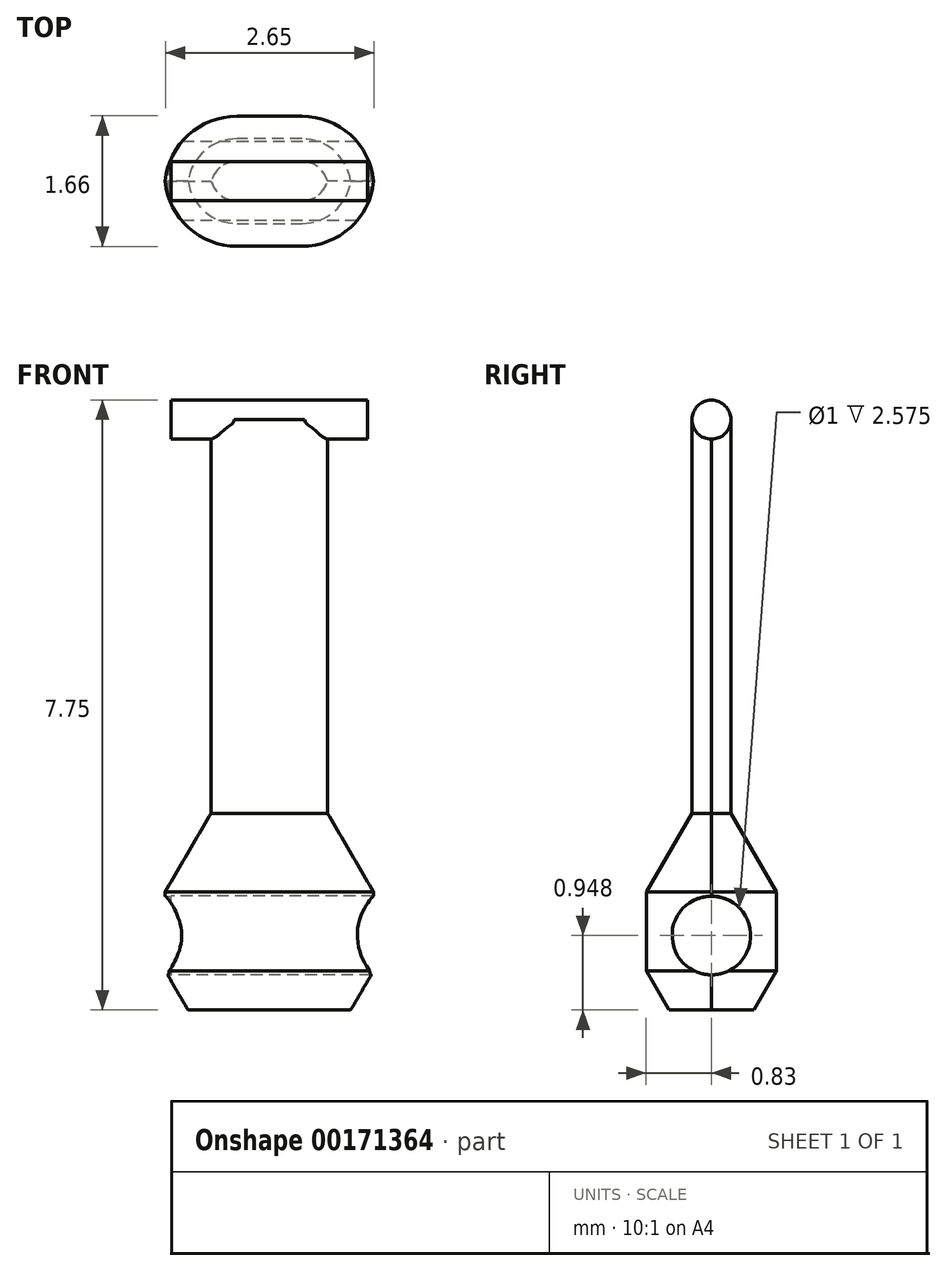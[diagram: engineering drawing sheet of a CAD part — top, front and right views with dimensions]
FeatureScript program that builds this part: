
annotation { "Feature Type Name" : "Feature", "Feature Type Description" : "" }
export const myFeature = defineFeature(function(context is Context, id is Id, definition is map)
    precondition{}
    {
        {
            var Q0;
            Q0=qCreatedBy(makeId("Right.planeOp"),FACE);
            var sketch = newSketch(context, id + "F0", { "sketchPlane" : qUnion([Q0])});
            skCircle(sketch, "E0", {"center": v(0, 0) * mm, "radius": 0.25 * mm});
            skSolve(sketch);
        }
        {
            var Q0;
            Q0=makeQuery(id+"F0.imprint","IMPRINT",FACE,{"disambiguationData":[TD([[makeQuery(id+"F0.imprint","IMPRINT",EDGE,{"derivedFrom":sQuery(id+"F0.wireOp",EDGE,"E0")}),1.0]])]});
            extrude(context, id + "F1", {"entities" : qUnion([Q0]), "depth" : 2.5 * mm});
        }
        {
            var Q0;
            Q0=qCreatedBy(makeId("Top.planeOp"),FACE);
            var sketch = newSketch(context, id + "F2", { "sketchPlane" : qUnion([Q0])});
            skPoint(sketch, "E1", {"position": v(1.25, 0) * mm});
            skPoint(sketch, "E2.start.orphan", {"position": v(0, -0.24) * mm});
            skPoint(sketch, "E3.bottom.end.orphan", {"position": v(1, 0.25) * mm});
            skPoint(sketch, "E3.left.start.orphan", {"position": v(1.5, 0.25) * mm});
            skPoint(sketch, "E3.top.end.orphan", {"position": v(1, -0.25) * mm});
            skPoint(sketch, "E3.top.start.orphan", {"position": v(1.5, -0.25) * mm});
            skLineSegment(sketch, "E4.bottom", {"start": v(2, 0.25) * mm, "end": v(0.5, 0.25) * mm});
            skLineSegment(sketch, "E4.top", {"start": v(2, -0.25) * mm, "end": v(0.5, -0.25) * mm});
            skLineSegment(sketch, "E4.left", {"start": v(2, 0.25) * mm, "end": v(2, -0.25) * mm});
            skLineSegment(sketch, "E4.right", {"start": v(0.5, 0.25) * mm, "end": v(0.5, -0.25) * mm});
            skSolve(sketch);
        }
        {
            var Q0;
            Q0 = qSketchRegion(id + "F2", true);
            extrude(context, id + "F3", {"entities" : qUnion([Q0]), "operationType" : NewBodyOperationType.ADD, "oppositeDirection" : true, "depth" : 5 * mm});
        }
        {
            var Q0;
            Q0=makeQuery(id+"F3.opExtrude","SWEPT_EDGE",EDGE,{"disambiguationData":[OSD([sQuery(id+"F2.wireOp",EDGE,"E4.top"),sQuery(id+"F2.wireOp",EDGE,"E4.right")])]});
            var Q1;
            Q1=makeQuery(id+"F3.opExtrude","SWEPT_EDGE",EDGE,{"disambiguationData":[OSD([sQuery(id+"F2.wireOp",EDGE,"E4.bottom"),sQuery(id+"F2.wireOp",EDGE,"E4.right")])]});
            var Q2;
            Q2=makeQuery(id+"F3.opExtrude","SWEPT_EDGE",EDGE,{"disambiguationData":[OSD([sQuery(id+"F2.wireOp",EDGE,"E4.bottom"),sQuery(id+"F2.wireOp",EDGE,"E4.left")])]});
            var Q3;
            Q3=makeQuery(id+"F3.opExtrude","SWEPT_EDGE",EDGE,{"disambiguationData":[OSD([sQuery(id+"F2.wireOp",EDGE,"E4.top"),sQuery(id+"F2.wireOp",EDGE,"E4.left")])]});
            fillet(context, id + "F4", {"entities" : qUnion([Q0, Q1, Q2, Q3]), "radius" : 0.34 * mm, "tangentPropagation" : true, "allowEdgeOverflow" : false});
        }
        {
            var Q0;
            Q0=makeQuery(id+"F3.opExtrude","CAP_FACE",FACE,{"disambiguationData":[OSD([sQuery(id+"F2.wireOp",EDGE,"E4.bottom"),sQuery(id+"F2.wireOp",EDGE,"E4.top"),sQuery(id+"F2.wireOp",EDGE,"E4.left"),sQuery(id+"F2.wireOp",EDGE,"E4.right")])],"isStart":false});
            extrude(context, id + "F5", {"entities" : qUnion([Q0]), "operationType" : NewBodyOperationType.ADD, "depth" : 1 * mm, "hasDraft" : true, "draftAngle" : 30 * degree});
        }
        {
            var Q0;
            Q0=makeQuery(id+"F5.opExtrude","CAP_FACE",FACE,{"disambiguationData":[OSD([sQuery(id+"F2.wireOp",EDGE,"E4.bottom"),sQuery(id+"F2.wireOp",EDGE,"E4.top"),sQuery(id+"F2.wireOp",EDGE,"E4.left"),sQuery(id+"F2.wireOp",EDGE,"E4.right")])],"isStart":false});
            extrude(context, id + "F6", {"entities" : qUnion([Q0]), "operationType" : NewBodyOperationType.ADD, "depth" : 1 * mm});
        }
        {
            var Q0;
            Q0=makeQuery(id+"F6.opExtrude","CAP_FACE",FACE,{"disambiguationData":[OSD([sQuery(id+"F2.wireOp",EDGE,"E4.bottom"),sQuery(id+"F2.wireOp",EDGE,"E4.top"),sQuery(id+"F2.wireOp",EDGE,"E4.left"),sQuery(id+"F2.wireOp",EDGE,"E4.right")])],"isStart":false});
            extrude(context, id + "F7", {"entities" : qUnion([Q0]), "operationType" : NewBodyOperationType.ADD, "depth" : 0.5 * mm, "hasDraft" : true, "draftAngle" : 30 * degree, "draftPullDirection" : true});
        }
        {
            var Q0;
            Q0=qCreatedBy(makeId("Right.planeOp"),FACE);
            var sketch = newSketch(context, id + "F8", { "sketchPlane" : qUnion([Q0])});
            skPoint(sketch, "E5", {"position": v(0, -6.55) * mm});
            skSolve(sketch);
        }
        {
            var Q0;
            Q0=sQuery(id+"F8.wireOp",VERTEX,"E5");
            var Q1;
            Q1=makeQuery(id+"F1.opExtrude","SWEPT_BODY",BODY,{"disambiguationData":[OSD([sQuery(id+"F0.wireOp",EDGE,"E0")])]});
            hole(context, id + "F9", {"style" : HoleStyle.SIMPLE, "endStyle" : HoleEndStyle.THROUGH, "oppositeDirection" : true, "holeDiameter" : 1 * mm, "locations" : qUnion([Q0]), "scope" : qUnion([Q1]), "isTappedThrough" : true});
        }
        {
            var Q0;
            Q0=qCreatedBy(makeId("Right.planeOp"),FACE);
            var sketch = newSketch(context, id + "F10", { "sketchPlane" : qUnion([Q0])});
            skPoint(sketch, "E6", {"position": v(0, -6.55) * mm});
            skPoint(sketch, "E7.start.orphan", {"position": v(0, -6.06) * mm});
            skSolve(sketch);
        }
        {
            var Q0;
            Q0=sQuery(id+"F10.wireOp",VERTEX,"E6");
            var Q1;
            Q1=makeQuery(id+"F1.opExtrude","SWEPT_BODY",BODY,{"disambiguationData":[OSD([sQuery(id+"F0.wireOp",EDGE,"E0")])]});
            hole(context, id + "F11", {"style" : HoleStyle.SIMPLE, "endStyle" : HoleEndStyle.THROUGH, "holeDiameter" : 1 * mm, "locations" : qUnion([Q0]), "scope" : qUnion([Q1]), "isTappedThrough" : true});
        }
    });
